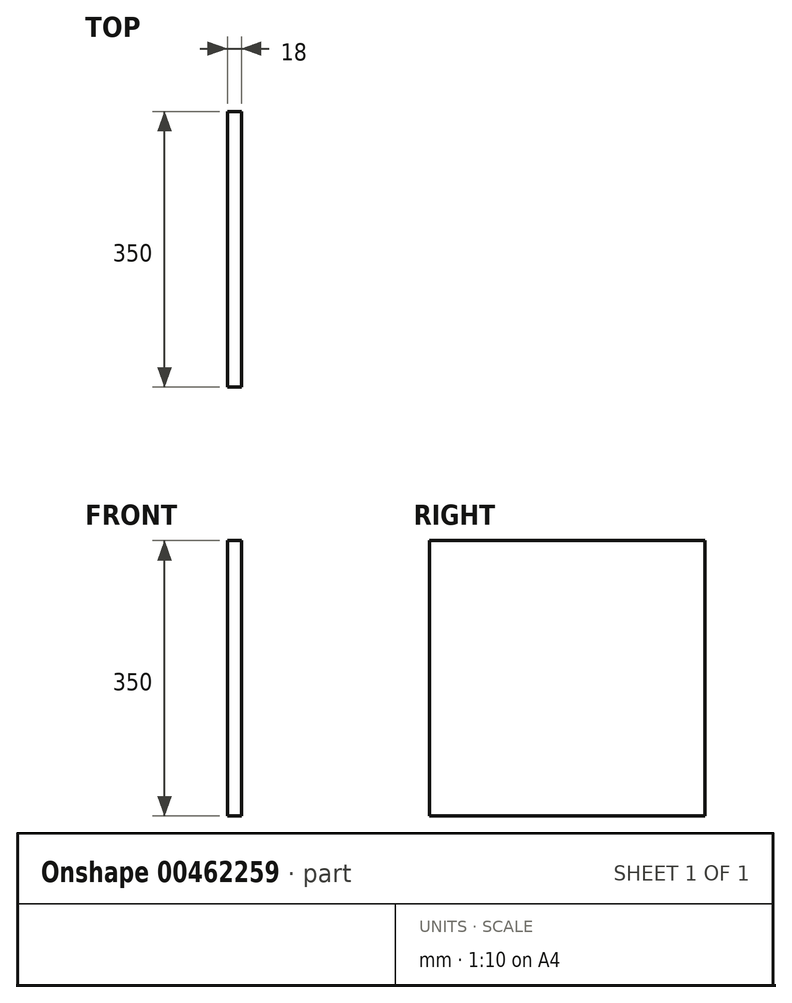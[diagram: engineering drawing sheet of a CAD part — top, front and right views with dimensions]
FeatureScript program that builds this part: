
annotation { "Feature Type Name" : "Feature", "Feature Type Description" : "" }
export const myFeature = defineFeature(function(context is Context, id is Id, definition is map)
    precondition{}
    {
        {
            var Q0;
            Q0=qCreatedBy(makeId("Top.planeOp"),FACE);
            var sketch = newSketch(context, id + "F0", { "sketchPlane" : qUnion([Q0])});
            skLineSegment(sketch, "E0.bottom", {"start": v(12.34, -175) * mm, "end": v(-5.66, -175) * mm});
            skLineSegment(sketch, "E0.top", {"start": v(12.34, 175) * mm, "end": v(-5.66, 175) * mm});
            skLineSegment(sketch, "E0.left", {"start": v(12.34, -175) * mm, "end": v(12.34, 175) * mm});
            skLineSegment(sketch, "E0.right", {"start": v(-5.66, -175) * mm, "end": v(-5.66, 175) * mm});
            skPoint(sketch, "E0.middle", {"position": v(3.34, 0) * mm});
            skSolve(sketch);
        }
        {
            var Q0;
            Q0=makeQuery(id+"F0.imprint","IMPRINT",FACE,{"disambiguationData":[TD([[makeQuery(id+"F0.imprint","IMPRINT",EDGE,{"derivedFrom":sQuery(id+"F0.wireOp",EDGE,"E0.bottom")}),-1.0]])]});
            extrude(context, id + "F1", {"entities" : qUnion([Q0]), "depth" : 350 * mm});
        }
    });
